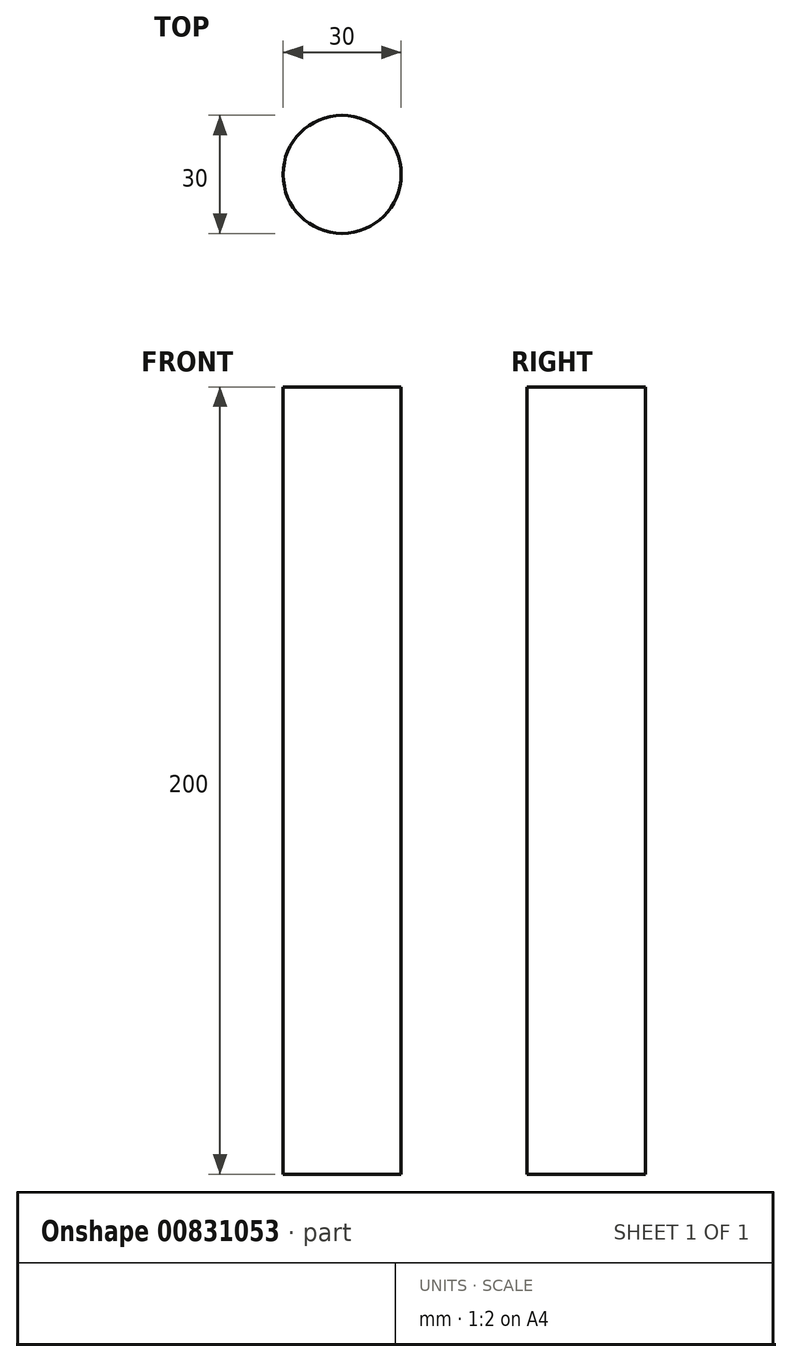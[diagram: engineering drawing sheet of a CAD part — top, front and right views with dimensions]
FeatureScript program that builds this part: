
annotation { "Feature Type Name" : "Feature", "Feature Type Description" : "" }
export const myFeature = defineFeature(function(context is Context, id is Id, definition is map)
    precondition{}
    {
        {
            var Q0;
            Q0=qCreatedBy(makeId("Top.planeOp"),FACE);
            var sketch = newSketch(context, id + "F0", { "sketchPlane" : qUnion([Q0])});
            skCircle(sketch, "E0", {"center": v(0, 0) * mm, "radius": 15 * mm});
            skSolve(sketch);
        }
        {
            var Q0;
            Q0 = qSketchRegion(id + "F0", true);
            var Q1;
            Q1=makeQuery(id+"F0.imprint","IMPRINT",FACE,{"disambiguationData":[TD([[makeQuery(id+"F0.imprint","IMPRINT",EDGE,{"derivedFrom":sQuery(id+"F0.wireOp",EDGE,"E0")}),1.0]])]});
            extrude(context, id + "F1", {"entities" : qUnion([Q0, Q1]), "depth" : 200 * mm, "offsetDistance" : 25 * mm});
        }
    });
